# Revit family: Sanitary_Urinals_Sanindusa_Wca_Urinal
name_source: partatom
category: Plumbing Fixtures
revit_build: Autodesk Revit 2018 (Build: 20170223_1515(x64)
units: mm (PartAtom-declared; Revit-internal decimal feet)

## family parameters
Cut with Voids When Loaded = No
Host = Face
Part Type = Normal
Room Calculation Point = No
Round Connector Dimension = Use Diameter
Shared = No

## types (1)
- Sanitary_Urinals_Sanindusa_Wca_Urinal
    AssetType = Fixed
    Category = Pr_40_20_93_78: Urinal Cisterns
    CodePerformance = EN 13407:2015
    Color = White
    Constituents = Package content:
Urinal, installation kit, urinal bung flushpipe connector, siphon trap for urinal, fixing kit and assembly instructions. Complements (not included): 5410571–Unit urinal electronic tap with battery; 5410581–Unit urinal electronic tap with transformer; 5120571–Plan urinal electronic tap with battery; 5120581–Plan urinal electronic tap with transformer; 5190541–Eco concealed timer tap for urinal; 5195741–Eco Concealed timer tap w/ medical lever for Urinal.
    Default Elevation = 1219 mm
    Description = Soil appliance that receives urine and directs it to a waste outlet (BS6100)
    DrainSize = 50 mm  [stored 0.164042 ft]
    Element Type = URINAL: Soil appliance that receives urine and directs it to a waste outlet (BS6100)
    Features = Compact, ideal for small, public and private spaces
Easy installation and maintenance
Gathers aesthetics and functionality in a quality ceramic tile.
    Finish = gloss
    InletDiameter = 13 mm
    Installation Instructions = https://www.tec.sanindusa.pt
    InstallationDate = 1900-12-31T23:59:59
    Manufacturer = Sanindusa
    ManufacturerName = Sanindusa
    ManufacturerURL = www.tec.sanindusa.pt
    Material = Vitreous China
    Model = 111500004
    ModelNumber = 111500004
    ModelReference = Wca
    Name = Urinal wca
    NominalHeight = 505 mm  [stored 1.65682 ft]
    NominalLength = 350 mm  [stored 1.14829 ft]
    NominalWidth = 315 mm  [stored 1.03346 ft]
    Pre-defined type (IFC) = URINAL
    ProductInformation = https://www.tec.sanindusa.pt
    ProductionYear = 2019
    Type (IFC) = IfcSanitaryTerminalType
    URL = www.tec.sanindusa.pt
    Version = 1
    WarrantyDescription = https://www.tec.sanindusa.pt
    WarrantyDurationParts = 5
    WarrantyDurationUnit = year
    WarrantyStartDate = 1900-12-31T23:59:59
    Weight = 13.80 kg

note: [stored X ft] marks values corroborated as IEEE doubles in the binary element streams (Revit-internal decimal feet)

## geometry (parser evidence)
native form markers: Sweep x7
no freeform markers — native parametric forms only
